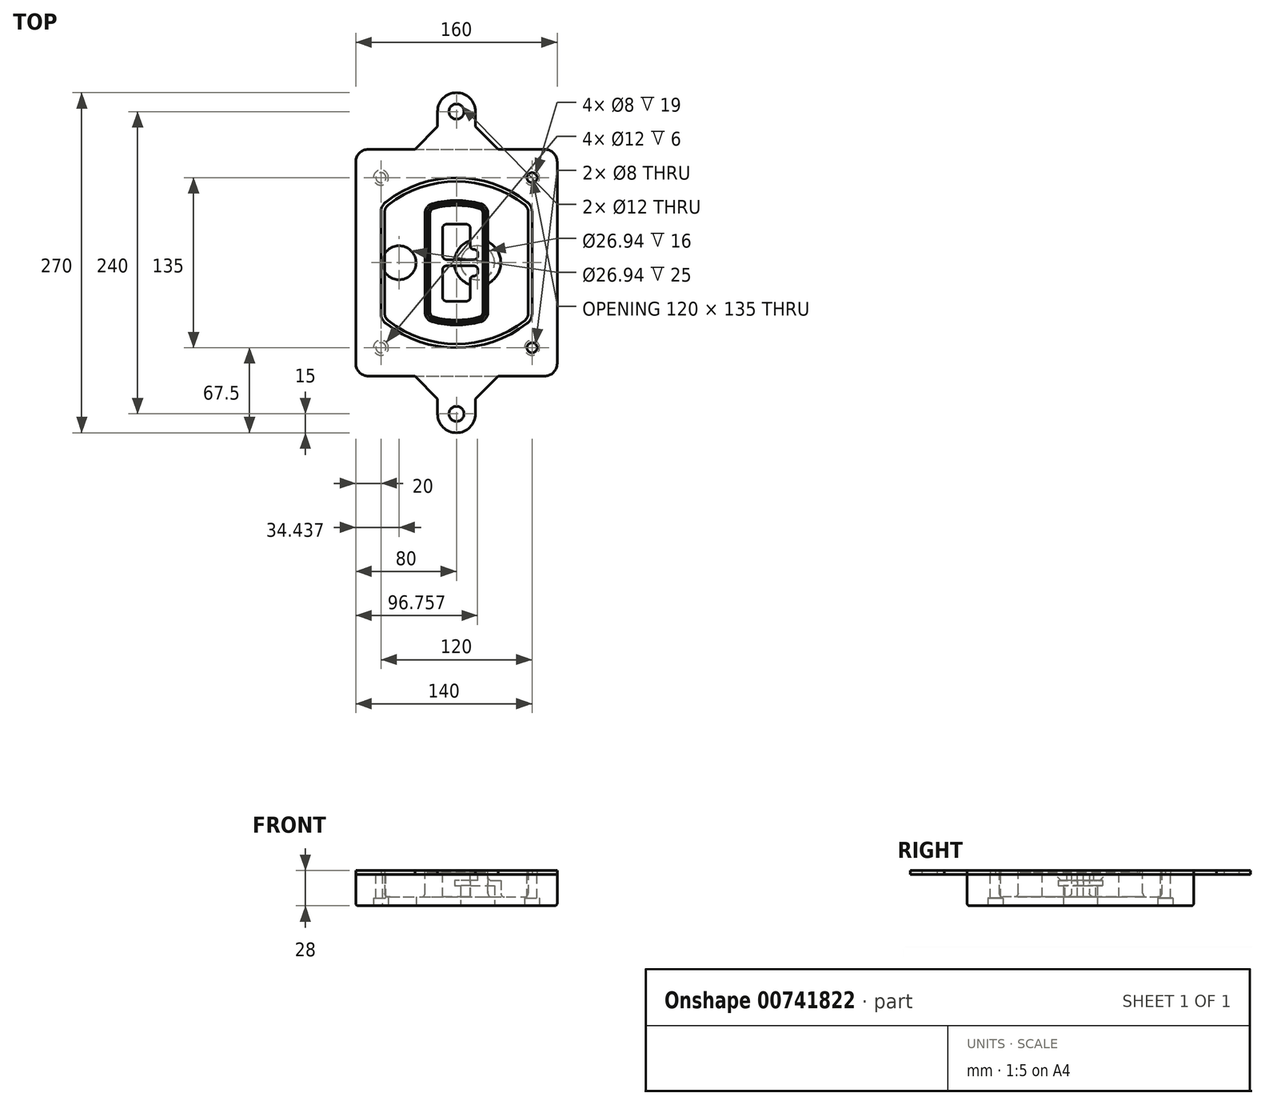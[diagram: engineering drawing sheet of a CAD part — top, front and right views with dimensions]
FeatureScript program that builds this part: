
annotation { "Feature Type Name" : "Feature", "Feature Type Description" : "" }
export const myFeature = defineFeature(function(context is Context, id is Id, definition is map)
    precondition{}
    {
        {
            var Q0;
            Q0=qCreatedBy(makeId("Top.planeOp"),FACE);
            var sketch = newSketch(context, id + "F0", { "sketchPlane" : qUnion([Q0])});
            skPoint(sketch, "E0.rect.middle", {"position": v(0, 0) * mm});
            skLineSegment(sketch, "E1.bottom", {"start": v(-70, -90) * mm, "end": v(70, -90) * mm});
            skLineSegment(sketch, "E1.top", {"start": v(-70, 90) * mm, "end": v(70, 90) * mm});
            skLineSegment(sketch, "E1.left", {"start": v(-80, -80) * mm, "end": v(-80, 80) * mm});
            skLineSegment(sketch, "E1.right", {"start": v(80, -80) * mm, "end": v(80, 80) * mm});
            skLineSegment(sketch, "E2", {"start": v(-80, 90) * mm, "end": v(80, -90) * mm, "construction": true});
            skLineSegment(sketch, "E3", {"start": v(80, 90) * mm, "end": v(-80, -90) * mm, "construction": true});
            skCircle(sketch, "E4", {"center": v(-60, 67.5) * mm, "radius": 4 * mm});
            skCircle(sketch, "E5", {"center": v(60, 67.5) * mm, "radius": 4 * mm});
            skCircle(sketch, "E6", {"center": v(60, -67.5) * mm, "radius": 4 * mm});
            skCircle(sketch, "E7", {"center": v(-60, -67.5) * mm, "radius": 4 * mm});
            skLineSegment(sketch, "E8", {"start": v(-60, 67.5) * mm, "end": v(60, 67.5) * mm, "construction": true});
            skLineSegment(sketch, "E9", {"start": v(60, 67.5) * mm, "end": v(60, -67.5) * mm, "construction": true});
            skLineSegment(sketch, "E10", {"start": v(60, -67.5) * mm, "end": v(-60, -67.5) * mm, "construction": true});
            skLineSegment(sketch, "E11", {"start": v(-60, -67.5) * mm, "end": v(-60, 67.5) * mm, "construction": true});
            skLineSegment(sketch, "E12", {"start": v(-60, 40.3) * mm, "end": v(-60, -40.3) * mm});
            skLineSegment(sketch, "E13", {"start": v(60, 40.3) * mm, "end": v(60, -40.3) * mm});
            skArc(sketch, "E14", {"start": v(56.15, 48.18) * mm, "mid": v(0, 67.5) * mm, "end": v(-56.15, 48.18) * mm});
            skArc(sketch, "E15", {"start": v(-56.15, -48.18) * mm, "mid": v(0, -67.5) * mm, "end": v(56.15, -48.18) * mm});
            skLineSegment(sketch, "E16", {"start": v(-60, 0) * mm, "end": v(60, 0) * mm, "construction": true});
            skPoint(sketch, "E17.visualSharp", {"position": v(-60, -45) * mm});
            skArc(sketch, "E17.filletArc", {"start": v(-60, -40.3) * mm, "mid": v(-58.99, -44.68) * mm, "end": v(-56.15, -48.18) * mm});
            skPoint(sketch, "E18.visualSharp", {"position": v(-60, 45) * mm});
            skArc(sketch, "E18.filletArc", {"start": v(-56.15, 48.18) * mm, "mid": v(-58.99, 44.68) * mm, "end": v(-60, 40.3) * mm});
            skPoint(sketch, "E19.visualSharp", {"position": v(60, 45) * mm});
            skArc(sketch, "E19.filletArc", {"start": v(60, 40.3) * mm, "mid": v(58.99, 44.68) * mm, "end": v(56.15, 48.18) * mm});
            skPoint(sketch, "E20.visualSharp", {"position": v(60, -45) * mm});
            skArc(sketch, "E20.filletArc", {"start": v(56.15, -48.18) * mm, "mid": v(58.99, -44.68) * mm, "end": v(60, -40.3) * mm});
            skPoint(sketch, "E21.visualSharp", {"position": v(-80, 90) * mm});
            skArc(sketch, "E21.filletArc", {"start": v(-70, 90) * mm, "mid": v(-77.07, 87.07) * mm, "end": v(-80, 80) * mm});
            skPoint(sketch, "E22.visualSharp", {"position": v(80, 90) * mm});
            skArc(sketch, "E22.filletArc", {"start": v(80, 80) * mm, "mid": v(77.07, 87.07) * mm, "end": v(70, 90) * mm});
            skPoint(sketch, "E23.visualSharp", {"position": v(80, -90) * mm});
            skArc(sketch, "E23.filletArc", {"start": v(70, -90) * mm, "mid": v(77.07, -87.07) * mm, "end": v(80, -80) * mm});
            skPoint(sketch, "E24.visualSharp", {"position": v(-80, -90) * mm});
            skArc(sketch, "E24.filletArc", {"start": v(-80, -80) * mm, "mid": v(-77.07, -87.07) * mm, "end": v(-70, -90) * mm});
            skArc(sketch, "E25.0", {"start": v(57, 40.3) * mm, "mid": v(56.3, 43.36) * mm, "end": v(54.3, 45.81) * mm});
            skLineSegment(sketch, "E25.1", {"start": v(57, 40.3) * mm, "end": v(57, -40.3) * mm});
            skArc(sketch, "E25.2", {"start": v(54.3, -45.81) * mm, "mid": v(56.3, -43.36) * mm, "end": v(57, -40.3) * mm});
            skArc(sketch, "E25.3", {"start": v(-54.3, -45.81) * mm, "mid": v(0, -64.5) * mm, "end": v(54.3, -45.81) * mm});
            skArc(sketch, "E25.4", {"start": v(-57, -40.3) * mm, "mid": v(-56.3, -43.36) * mm, "end": v(-54.3, -45.81) * mm});
            skArc(sketch, "E25.5", {"start": v(54.3, 45.81) * mm, "mid": v(0, 64.5) * mm, "end": v(-54.3, 45.81) * mm});
            skLineSegment(sketch, "E25.6", {"start": v(-57, 40.3) * mm, "end": v(-57, -40.3) * mm});
            skArc(sketch, "E25.7", {"start": v(-54.3, 45.81) * mm, "mid": v(-56.3, 43.36) * mm, "end": v(-57, 40.3) * mm});
            skArc(sketch, "E26.0", {"start": v(-58.62, 51.33) * mm, "mid": v(-62.58, 46.43) * mm, "end": v(-64, 40.3) * mm});
            skArc(sketch, "E26.1", {"start": v(58.62, 51.33) * mm, "mid": v(0, 71.5) * mm, "end": v(-58.62, 51.33) * mm});
            skArc(sketch, "E26.2", {"start": v(64, 40.3) * mm, "mid": v(62.58, 46.43) * mm, "end": v(58.62, 51.33) * mm});
            skLineSegment(sketch, "E26.3", {"start": v(64, 40.3) * mm, "end": v(64, -40.3) * mm});
            skArc(sketch, "E26.4", {"start": v(58.62, -51.33) * mm, "mid": v(62.58, -46.43) * mm, "end": v(64, -40.3) * mm});
            skLineSegment(sketch, "E26.5", {"start": v(-64, 40.3) * mm, "end": v(-64, -40.3) * mm});
            skArc(sketch, "E26.6", {"start": v(-58.62, -51.33) * mm, "mid": v(0, -71.5) * mm, "end": v(58.62, -51.33) * mm});
            skArc(sketch, "E26.7", {"start": v(-64, -40.3) * mm, "mid": v(-62.58, -46.43) * mm, "end": v(-58.62, -51.33) * mm});
            skSolve(sketch);
        }
        {
            var Q0;
            Q0=makeQuery(id+"F0.imprint","IMPRINT",FACE,{"disambiguationData":[TD([[makeQuery(id+"F0.imprint","IMPRINT",EDGE,{"derivedFrom":sQuery(id+"F0.wireOp",EDGE,"E1.bottom")}),1.0]])]});
            var Q1;
            Q1=makeQuery(id+"F0.imprint","IMPRINT",FACE,{"disambiguationData":[TD([[makeQuery(id+"F0.imprint","IMPRINT",EDGE,{"derivedFrom":sQuery(id+"F0.wireOp",EDGE,"E12")}),1.0]])]});
            var Q2;
            Q2=makeQuery(id+"F0.imprint","IMPRINT",FACE,{"disambiguationData":[TD([[makeQuery(id+"F0.imprint","IMPRINT",EDGE,{"derivedFrom":sQuery(id+"F0.wireOp",EDGE,"E25.0")}),1.0]])]});
            var Q3;
            Q3=makeQuery(id+"F0.imprint","IMPRINT",FACE,{"disambiguationData":[TD([[makeQuery(id+"F0.imprint","IMPRINT",EDGE,{"derivedFrom":sQuery(id+"F0.wireOp",EDGE,"E12")}),-1.0]])]});
            extrude(context, id + "F1", {"entities" : qUnion([Q0, Q1, Q2, Q3]), "oppositeDirection" : true, "depth" : 25 * mm});
        }
        {
            var Q0;
            Q0=makeQuery(id+"F0.imprint","IMPRINT",FACE,{"disambiguationData":[TD([[makeQuery(id+"F0.imprint","IMPRINT",EDGE,{"derivedFrom":sQuery(id+"F0.wireOp",EDGE,"E12")}),1.0]])]});
            extrude(context, id + "F2", {"entities" : qUnion([Q0]), "operationType" : NewBodyOperationType.ADD, "depth" : 3 * mm});
        }
        {
            var Q0;
            Q0=makeQuery(id+"F0.imprint","IMPRINT",FACE,{"disambiguationData":[TD([[makeQuery(id+"F0.imprint","IMPRINT",EDGE,{"derivedFrom":sQuery(id+"F0.wireOp",EDGE,"E25.0")}),1.0]])]});
            extrude(context, id + "F3", {"entities" : qUnion([Q0]), "operationType" : NewBodyOperationType.REMOVE, "oppositeDirection" : true, "depth" : 18 * mm});
        }
        {
            var Q0;
            Q0=makeQuery(id+"F2.opExtrude","CAP_FACE",FACE,{"disambiguationData":[OSD([sQuery(id+"F0.wireOp",EDGE,"E12"),sQuery(id+"F0.wireOp",EDGE,"E13"),sQuery(id+"F0.wireOp",EDGE,"E14"),sQuery(id+"F0.wireOp",EDGE,"E15"),sQuery(id+"F0.wireOp",EDGE,"E17.filletArc"),sQuery(id+"F0.wireOp",EDGE,"E18.filletArc"),sQuery(id+"F0.wireOp",EDGE,"E19.filletArc"),sQuery(id+"F0.wireOp",EDGE,"E20.filletArc"),sQuery(id+"F0.wireOp",EDGE,"E25.0"),sQuery(id+"F0.wireOp",EDGE,"E25.1"),sQuery(id+"F0.wireOp",EDGE,"E25.2"),sQuery(id+"F0.wireOp",EDGE,"E25.3"),sQuery(id+"F0.wireOp",EDGE,"E25.4"),sQuery(id+"F0.wireOp",EDGE,"E25.5"),sQuery(id+"F0.wireOp",EDGE,"E25.6"),sQuery(id+"F0.wireOp",EDGE,"E25.7")])],"isStart":false});
            var sketch = newSketch(context, id + "F4", { "sketchPlane" : qUnion([Q0])});
            skArc(sketch, "E27.0", {"start": v(-19.08, -46.97) * mm, "mid": v(0, -49.5) * mm, "end": v(19.08, -46.97) * mm});
            skArc(sketch, "E28.0", {"start": v(19.08, 46.97) * mm, "mid": v(0, 49.5) * mm, "end": v(-19.08, 46.97) * mm});
            skLineSegment(sketch, "E29", {"start": v(-25, 39.25) * mm, "end": v(-25, -39.25) * mm});
            skLineSegment(sketch, "E30", {"start": v(25, 39.25) * mm, "end": v(25, -39.25) * mm});
            skLineSegment(sketch, "E31", {"start": v(-25, 45.1) * mm, "end": v(25, 45.1) * mm, "construction": true});
            skLineSegment(sketch, "E32", {"start": v(-25, -45.1) * mm, "end": v(25, -45.1) * mm, "construction": true});
            skPoint(sketch, "E33.visualSharp", {"position": v(-25, 45.1) * mm});
            skArc(sketch, "E33.filletArc", {"start": v(-19.08, 46.97) * mm, "mid": v(-23.35, 44.11) * mm, "end": v(-25, 39.25) * mm});
            skPoint(sketch, "E34.visualSharp", {"position": v(25, 45.1) * mm});
            skArc(sketch, "E34.filletArc", {"start": v(25, 39.25) * mm, "mid": v(23.35, 44.11) * mm, "end": v(19.08, 46.97) * mm});
            skPoint(sketch, "E35.visualSharp", {"position": v(25, -45.1) * mm});
            skArc(sketch, "E35.filletArc", {"start": v(19.08, -46.97) * mm, "mid": v(23.35, -44.11) * mm, "end": v(25, -39.25) * mm});
            skPoint(sketch, "E36.visualSharp", {"position": v(-25, -45.1) * mm});
            skArc(sketch, "E36.filletArc", {"start": v(-25, -39.25) * mm, "mid": v(-23.35, -44.11) * mm, "end": v(-19.08, -46.97) * mm});
            skArc(sketch, "E37.0", {"start": v(54.3, 45.81) * mm, "mid": v(0, 64.5) * mm, "end": v(-54.3, 45.81) * mm});
            skArc(sketch, "E37.1", {"start": v(-54.3, 45.81) * mm, "mid": v(-56.3, 43.36) * mm, "end": v(-57, 40.3) * mm});
            skLineSegment(sketch, "E37.2", {"start": v(-57, 40.3) * mm, "end": v(-57, -40.3) * mm});
            skArc(sketch, "E37.3", {"start": v(-57, -40.3) * mm, "mid": v(-56.3, -43.36) * mm, "end": v(-54.3, -45.81) * mm});
            skArc(sketch, "E37.4", {"start": v(-54.3, -45.81) * mm, "mid": v(0, -64.5) * mm, "end": v(54.3, -45.81) * mm});
            skArc(sketch, "E37.5", {"start": v(54.3, -45.81) * mm, "mid": v(56.3, -43.36) * mm, "end": v(57, -40.3) * mm});
            skLineSegment(sketch, "E37.6", {"start": v(57, 40.3) * mm, "end": v(57, -40.3) * mm});
            skArc(sketch, "E37.7", {"start": v(57, 40.3) * mm, "mid": v(56.3, 43.36) * mm, "end": v(54.3, 45.81) * mm});
            skLineSegment(sketch, "E38.0", {"start": v(23, 39.25) * mm, "end": v(23, -39.25) * mm});
            skArc(sketch, "E38.1", {"start": v(18.56, -45.04) * mm, "mid": v(21.76, -42.9) * mm, "end": v(23, -39.25) * mm});
            skArc(sketch, "E38.2", {"start": v(-18.56, -45.04) * mm, "mid": v(0, -47.5) * mm, "end": v(18.56, -45.04) * mm});
            skArc(sketch, "E38.3", {"start": v(-23, -39.25) * mm, "mid": v(-21.76, -42.9) * mm, "end": v(-18.56, -45.04) * mm});
            skLineSegment(sketch, "E38.4", {"start": v(-23, 39.25) * mm, "end": v(-23, -39.25) * mm});
            skArc(sketch, "E38.5", {"start": v(23, 39.25) * mm, "mid": v(21.76, 42.9) * mm, "end": v(18.56, 45.04) * mm});
            skArc(sketch, "E38.6", {"start": v(-18.56, 45.04) * mm, "mid": v(-21.76, 42.9) * mm, "end": v(-23, 39.25) * mm});
            skArc(sketch, "E38.7", {"start": v(18.56, 45.04) * mm, "mid": v(0, 47.5) * mm, "end": v(-18.56, 45.04) * mm});
            skArc(sketch, "E39.0", {"start": v(21, 39.25) * mm, "mid": v(20.18, 41.68) * mm, "end": v(18.04, 43.1) * mm});
            skLineSegment(sketch, "E39.1", {"start": v(21, 39.25) * mm, "end": v(21, -39.25) * mm});
            skArc(sketch, "E39.2", {"start": v(18.04, -43.1) * mm, "mid": v(20.18, -41.68) * mm, "end": v(21, -39.25) * mm});
            skArc(sketch, "E39.3", {"start": v(-18.04, -43.1) * mm, "mid": v(0, -45.5) * mm, "end": v(18.04, -43.1) * mm});
            skArc(sketch, "E39.4", {"start": v(-21, -39.25) * mm, "mid": v(-20.18, -41.68) * mm, "end": v(-18.04, -43.1) * mm});
            skArc(sketch, "E39.5", {"start": v(18.04, 43.1) * mm, "mid": v(0, 45.5) * mm, "end": v(-18.04, 43.1) * mm});
            skLineSegment(sketch, "E39.6", {"start": v(-21, 39.25) * mm, "end": v(-21, -39.25) * mm});
            skArc(sketch, "E39.7", {"start": v(-18.04, 43.1) * mm, "mid": v(-20.18, 41.68) * mm, "end": v(-21, 39.25) * mm});
            skLineSegment(sketch, "E40", {"start": v(-25, 0) * mm, "end": v(25, 0) * mm, "construction": true});
            skLineSegment(sketch, "E41", {"start": v(-11, 5.5) * mm, "end": v(-11, 27.5) * mm});
            skLineSegment(sketch, "E42", {"start": v(-8, 30.5) * mm, "end": v(8, 30.5) * mm});
            skLineSegment(sketch, "E43", {"start": v(11, 27.5) * mm, "end": v(11, 13.5) * mm});
            skLineSegment(sketch, "E44", {"start": v(14, 10.5) * mm, "end": v(14, 10.5) * mm});
            skLineSegment(sketch, "E45", {"start": v(17, 7.5) * mm, "end": v(17, 5.5) * mm});
            skLineSegment(sketch, "E46", {"start": v(14, 2.5) * mm, "end": v(-8, 2.5) * mm});
            skPoint(sketch, "E47.visualSharp", {"position": v(-11, 30.5) * mm});
            skArc(sketch, "E47.filletArc", {"start": v(-8, 30.5) * mm, "mid": v(-10.12, 29.62) * mm, "end": v(-11, 27.5) * mm});
            skPoint(sketch, "E48.visualSharp", {"position": v(11, 30.5) * mm});
            skArc(sketch, "E48.filletArc", {"start": v(11, 27.5) * mm, "mid": v(10.12, 29.62) * mm, "end": v(8, 30.5) * mm});
            skPoint(sketch, "E49.visualSharp", {"position": v(11, 10.5) * mm});
            skArc(sketch, "E49.filletArc", {"start": v(11, 13.5) * mm, "mid": v(11.88, 11.38) * mm, "end": v(14, 10.5) * mm});
            skPoint(sketch, "E50.visualSharp", {"position": v(17, 10.5) * mm});
            skArc(sketch, "E50.filletArc", {"start": v(17, 7.5) * mm, "mid": v(16.12, 9.62) * mm, "end": v(14, 10.5) * mm});
            skPoint(sketch, "E51.visualSharp", {"position": v(17, 2.5) * mm});
            skArc(sketch, "E51.filletArc", {"start": v(14, 2.5) * mm, "mid": v(16.12, 3.38) * mm, "end": v(17, 5.5) * mm});
            skPoint(sketch, "E52.visualSharp", {"position": v(-11, 2.5) * mm});
            skArc(sketch, "E52.filletArc", {"start": v(-11, 5.5) * mm, "mid": v(-10.12, 3.38) * mm, "end": v(-8, 2.5) * mm});
            skLineSegment(sketch, "E53.0.MirrorCS", {"start": v(14, -2.5) * mm, "end": v(-8, -2.5) * mm});
            skArc(sketch, "E54.0.MirrorCS", {"start": v(-11, -5.5) * mm, "mid": v(-10.12, -3.38) * mm, "end": v(-8, -2.5) * mm});
            skLineSegment(sketch, "E55.0.MirrorCS", {"start": v(-11, -5.5) * mm, "end": v(-11, -27.5) * mm});
            skArc(sketch, "E56.0.MirrorCS", {"start": v(-8, -30.5) * mm, "mid": v(-10.12, -29.62) * mm, "end": v(-11, -27.5) * mm});
            skLineSegment(sketch, "E57.0.MirrorCS", {"start": v(-8, -30.5) * mm, "end": v(8, -30.5) * mm});
            skArc(sketch, "E58.0.MirrorCS", {"start": v(11, -27.5) * mm, "mid": v(10.12, -29.62) * mm, "end": v(8, -30.5) * mm});
            skLineSegment(sketch, "E59.0.MirrorCS", {"start": v(11, -27.5) * mm, "end": v(11, -13.5) * mm});
            skArc(sketch, "E60.0.MirrorCS", {"start": v(11, -13.5) * mm, "mid": v(11.88, -11.38) * mm, "end": v(14, -10.5) * mm});
            skArc(sketch, "E61.0.MirrorCS", {"start": v(17, -7.5) * mm, "mid": v(16.12, -9.62) * mm, "end": v(14, -10.5) * mm});
            skLineSegment(sketch, "E62.0.MirrorCS", {"start": v(17, -7.5) * mm, "end": v(17, -5.5) * mm});
            skArc(sketch, "E63.0.MirrorCS", {"start": v(14, -2.5) * mm, "mid": v(16.12, -3.38) * mm, "end": v(17, -5.5) * mm});
            skSolve(sketch);
        }
        {
            var Q0;
            Q0=makeQuery(id+"F4.imprint","IMPRINT",FACE,{"disambiguationData":[TD([[makeQuery(id+"F4.imprint","IMPRINT",EDGE,{"derivedFrom":sQuery(id+"F4.wireOp",EDGE,"E27.0")}),1.0]])]});
            var Q1;
            Q1=makeQuery(id+"F4.imprint","IMPRINT",FACE,{"disambiguationData":[TD([[makeQuery(id+"F4.imprint","IMPRINT",EDGE,{"derivedFrom":sQuery(id+"F4.wireOp",EDGE,"E38.0")}),-1.0]])]});
            var Q2;
            Q2=makeQuery(id+"F4.imprint","IMPRINT",FACE,{"disambiguationData":[TD([[makeQuery(id+"F4.imprint","IMPRINT",EDGE,{"derivedFrom":sQuery(id+"F4.wireOp",EDGE,"E39.0")}),1.0]])]});
            extrude(context, id + "F5", {"entities" : qUnion([Q0, Q1, Q2]), "operationType" : NewBodyOperationType.ADD, "endBound" : BoundingType.UP_TO_NEXT, "oppositeDirection" : true, "depth" : 25 * mm});
        }
        {
            var Q0;
            Q0=makeQuery(id+"F4.imprint","IMPRINT",FACE,{"disambiguationData":[TD([[makeQuery(id+"F4.imprint","IMPRINT",EDGE,{"derivedFrom":sQuery(id+"F4.wireOp",EDGE,"E38.0")}),-1.0]])]});
            extrude(context, id + "F6", {"entities" : qUnion([Q0]), "operationType" : NewBodyOperationType.REMOVE, "oppositeDirection" : true, "depth" : 2 * mm});
        }
        {
            var Q0;
            Q0=makeQuery(id+"F1.opExtrude","CAP_FACE",FACE,{"disambiguationData":[OSD([sQuery(id+"F0.wireOp",EDGE,"E1.bottom"),sQuery(id+"F0.wireOp",EDGE,"E1.top"),sQuery(id+"F0.wireOp",EDGE,"E1.left"),sQuery(id+"F0.wireOp",EDGE,"E1.right"),sQuery(id+"F0.wireOp",EDGE,"E4"),sQuery(id+"F0.wireOp",EDGE,"E5"),sQuery(id+"F0.wireOp",EDGE,"E6"),sQuery(id+"F0.wireOp",EDGE,"E7"),sQuery(id+"F0.wireOp",EDGE,"E21.filletArc"),sQuery(id+"F0.wireOp",EDGE,"E22.filletArc"),sQuery(id+"F0.wireOp",EDGE,"E23.filletArc"),sQuery(id+"F0.wireOp",EDGE,"E24.filletArc")])],"isStart":false});
            var sketch = newSketch(context, id + "F7", { "sketchPlane" : qUnion([Q0])});
            skCircle(sketch, "E64", {"center": v(16.76, 0) * mm, "radius": 13.47 * mm});
            skCircle(sketch, "E65", {"center": v(-45.56, 0) * mm, "radius": 13.47 * mm});
            skLineSegment(sketch, "E66", {"start": v(80, 0) * mm, "end": v(-80, 0) * mm});
            skCircle(sketch, "E67", {"center": v(16.76, 0) * mm, "radius": 18.47 * mm});
            skCircle(sketch, "E68", {"center": v(60, -67.5) * mm, "radius": 6 * mm});
            skCircle(sketch, "E69", {"center": v(-60, -67.5) * mm, "radius": 6 * mm});
            skCircle(sketch, "E70", {"center": v(-60, 67.5) * mm, "radius": 6 * mm});
            skCircle(sketch, "E71", {"center": v(60, 67.5) * mm, "radius": 6 * mm});
            skSolve(sketch);
        }
        {
            var Q0;
            {var subQ1=sQuery(id+"F7.wireOp",EDGE,"E66");var subQ4=sQuery(id+"F7.wireOp",EDGE,"E64");var subQ6=makeQuery(id+"F7.imprint","INTERSECT",VERTEX,{"disambiguationData":[OD(0.0)],"derivedFrom":[subQ4,subQ1]});Q0=makeQuery(id+"F7.imprint","IMPRINT",FACE,{"disambiguationData":[TD([[makeQuery(id+"F7.imprint","IMPRINT",EDGE,{"disambiguationData":[TD([[subQ6,-1.0]])],"derivedFrom":subQ4}),-1.0]])]});}
            var Q1;
            {var subQ0=sQuery(id+"F7.wireOp",EDGE,"E66");var subQ1=sQuery(id+"F7.wireOp",EDGE,"E64");var subQ3=makeQuery(id+"F7.imprint","INTERSECT",VERTEX,{"disambiguationData":[OD(0.0)],"derivedFrom":[subQ1,subQ0]});Q1=makeQuery(id+"F7.imprint","IMPRINT",FACE,{"disambiguationData":[TD([[makeQuery(id+"F7.imprint","IMPRINT",EDGE,{"disambiguationData":[TD([[subQ3,-1.0]])],"derivedFrom":subQ1}),1.0]])]});}
            var Q2;
            {var subQ0=sQuery(id+"F7.wireOp",EDGE,"E66");var subQ1=sQuery(id+"F7.wireOp",EDGE,"E64");var subQ3=makeQuery(id+"F7.imprint","INTERSECT",VERTEX,{"disambiguationData":[OD(0.0)],"derivedFrom":[subQ1,subQ0]});Q2=makeQuery(id+"F7.imprint","IMPRINT",FACE,{"disambiguationData":[TD([[makeQuery(id+"F7.imprint","IMPRINT",EDGE,{"disambiguationData":[TD([[subQ3,1.0]])],"derivedFrom":subQ1}),1.0]])]});}
            var Q3;
            {var subQ1=sQuery(id+"F7.wireOp",EDGE,"E66");var subQ4=sQuery(id+"F7.wireOp",EDGE,"E64");var subQ6=makeQuery(id+"F7.imprint","INTERSECT",VERTEX,{"disambiguationData":[OD(0.0)],"derivedFrom":[subQ4,subQ1]});Q3=makeQuery(id+"F7.imprint","IMPRINT",FACE,{"disambiguationData":[TD([[makeQuery(id+"F7.imprint","IMPRINT",EDGE,{"disambiguationData":[TD([[subQ6,1.0]])],"derivedFrom":subQ4}),-1.0]])]});}
            extrude(context, id + "F8", {"entities" : qUnion([Q0, Q1, Q2, Q3]), "operationType" : NewBodyOperationType.ADD, "oppositeDirection" : true, "depth" : 20 * mm});
        }
        {
            var Q0;
            {var subQ0=sQuery(id+"F7.wireOp",EDGE,"E66");var subQ1=sQuery(id+"F7.wireOp",EDGE,"E64");var subQ3=makeQuery(id+"F7.imprint","INTERSECT",VERTEX,{"disambiguationData":[OD(0.0)],"derivedFrom":[subQ1,subQ0]});Q0=makeQuery(id+"F7.imprint","IMPRINT",FACE,{"disambiguationData":[TD([[makeQuery(id+"F7.imprint","IMPRINT",EDGE,{"disambiguationData":[TD([[subQ3,-1.0]])],"derivedFrom":subQ1}),1.0]])]});}
            var Q1;
            {var subQ0=sQuery(id+"F7.wireOp",EDGE,"E66");var subQ1=sQuery(id+"F7.wireOp",EDGE,"E64");var subQ3=makeQuery(id+"F7.imprint","INTERSECT",VERTEX,{"disambiguationData":[OD(0.0)],"derivedFrom":[subQ1,subQ0]});Q1=makeQuery(id+"F7.imprint","IMPRINT",FACE,{"disambiguationData":[TD([[makeQuery(id+"F7.imprint","IMPRINT",EDGE,{"disambiguationData":[TD([[subQ3,1.0]])],"derivedFrom":subQ1}),1.0]])]});}
            extrude(context, id + "F9", {"entities" : qUnion([Q0, Q1]), "operationType" : NewBodyOperationType.REMOVE, "oppositeDirection" : true, "depth" : 16 * mm});
        }
        {
            var Q0;
            {var subQ0=sQuery(id+"F7.wireOp",EDGE,"E66");var subQ1=sQuery(id+"F7.wireOp",EDGE,"E65");var subQ3=makeQuery(id+"F7.imprint","INTERSECT",VERTEX,{"disambiguationData":[OD(0.0)],"derivedFrom":[subQ1,subQ0]});Q0=makeQuery(id+"F7.imprint","IMPRINT",FACE,{"disambiguationData":[TD([[makeQuery(id+"F7.imprint","IMPRINT",EDGE,{"disambiguationData":[TD([[subQ3,-1.0]])],"derivedFrom":subQ1}),1.0]])]});}
            var Q1;
            {var subQ0=sQuery(id+"F7.wireOp",EDGE,"E66");var subQ1=sQuery(id+"F7.wireOp",EDGE,"E65");var subQ3=makeQuery(id+"F7.imprint","INTERSECT",VERTEX,{"disambiguationData":[OD(0.0)],"derivedFrom":[subQ1,subQ0]});Q1=makeQuery(id+"F7.imprint","IMPRINT",FACE,{"disambiguationData":[TD([[makeQuery(id+"F7.imprint","IMPRINT",EDGE,{"disambiguationData":[TD([[subQ3,1.0]])],"derivedFrom":subQ1}),1.0]])]});}
            extrude(context, id + "F10", {"entities" : qUnion([Q0, Q1]), "operationType" : NewBodyOperationType.REMOVE, "oppositeDirection" : true, "depth" : 25 * mm});
        }
        {
            var Q0;
            Q0=makeQuery(id+"F7.imprint","IMPRINT",FACE,{"disambiguationData":[TD([[makeQuery(id+"F7.imprint","IMPRINT",EDGE,{"derivedFrom":sQuery(id+"F7.wireOp",EDGE,"E68")}),1.0]])]});
            var Q1;
            Q1=makeQuery(id+"F7.imprint","IMPRINT",FACE,{"disambiguationData":[TD([[makeQuery(id+"F7.imprint","IMPRINT",EDGE,{"derivedFrom":makeQuery(id+"F1.opExtrude","CAP_EDGE",EDGE,{"disambiguationData":[OSD([sQuery(id+"F0.wireOp",EDGE,"E5")])],"isStart":false})}),-1.0]])]});
            var Q2;
            Q2=makeQuery(id+"F7.imprint","IMPRINT",FACE,{"disambiguationData":[TD([[makeQuery(id+"F7.imprint","IMPRINT",EDGE,{"derivedFrom":sQuery(id+"F7.wireOp",EDGE,"E69")}),1.0]])]});
            var Q3;
            Q3=makeQuery(id+"F7.imprint","IMPRINT",FACE,{"disambiguationData":[TD([[makeQuery(id+"F7.imprint","IMPRINT",EDGE,{"derivedFrom":makeQuery(id+"F1.opExtrude","CAP_EDGE",EDGE,{"disambiguationData":[OSD([sQuery(id+"F0.wireOp",EDGE,"E4")])],"isStart":false})}),-1.0]])]});
            var Q4;
            Q4=makeQuery(id+"F7.imprint","IMPRINT",FACE,{"disambiguationData":[TD([[makeQuery(id+"F7.imprint","IMPRINT",EDGE,{"derivedFrom":sQuery(id+"F7.wireOp",EDGE,"E70")}),1.0]])]});
            var Q5;
            Q5=makeQuery(id+"F7.imprint","IMPRINT",FACE,{"disambiguationData":[TD([[makeQuery(id+"F7.imprint","IMPRINT",EDGE,{"derivedFrom":makeQuery(id+"F1.opExtrude","CAP_EDGE",EDGE,{"disambiguationData":[OSD([sQuery(id+"F0.wireOp",EDGE,"E7")])],"isStart":false})}),-1.0]])]});
            var Q6;
            Q6=makeQuery(id+"F7.imprint","IMPRINT",FACE,{"disambiguationData":[TD([[makeQuery(id+"F7.imprint","IMPRINT",EDGE,{"derivedFrom":sQuery(id+"F7.wireOp",EDGE,"E71")}),1.0]])]});
            var Q7;
            Q7=makeQuery(id+"F7.imprint","IMPRINT",FACE,{"disambiguationData":[TD([[makeQuery(id+"F7.imprint","IMPRINT",EDGE,{"derivedFrom":makeQuery(id+"F1.opExtrude","CAP_EDGE",EDGE,{"disambiguationData":[OSD([sQuery(id+"F0.wireOp",EDGE,"E6")])],"isStart":false})}),-1.0]])]});
            extrude(context, id + "F11", {"entities" : qUnion([Q0, Q1, Q2, Q3, Q4, Q5, Q6, Q7]), "operationType" : NewBodyOperationType.REMOVE, "oppositeDirection" : true, "depth" : 6 * mm});
        }
        {
            var Q0;
            Q0=makeQuery(id+"F9.boolean.opBoolean","COPY",FACE,{"derivedFrom":makeQuery(id+"F9.opExtrude","CAP_FACE",FACE,{"disambiguationData":[OSD([sQuery(id+"F7.wireOp",EDGE,"E64")])],"isStart":false})});
            var sketch = newSketch(context, id + "F12", { "sketchPlane" : qUnion([Q0])});
            skArc(sketch, "E72.0", {"start": v(11, 17.55) * mm, "mid": v(2.57, 11.82) * mm, "end": v(-1.54, 2.5) * mm});
            skArc(sketch, "E72.1", {"start": v(-1.54, -2.5) * mm, "mid": v(2.57, -11.82) * mm, "end": v(11, -17.55) * mm});
            skLineSegment(sketch, "E73", {"start": v(-1.54, -2.5) * mm, "end": v(14, -2.5) * mm});
            skLineSegment(sketch, "E74.0", {"start": v(14, 2.5) * mm, "end": v(-1.54, 2.5) * mm});
            skArc(sketch, "E74.1", {"start": v(14, 2.5) * mm, "mid": v(16.12, 3.38) * mm, "end": v(17, 5.5) * mm});
            skLineSegment(sketch, "E74.2", {"start": v(17, 7.5) * mm, "end": v(17, 5.5) * mm});
            skArc(sketch, "E74.3", {"start": v(17, 7.5) * mm, "mid": v(16.12, 9.62) * mm, "end": v(14, 10.5) * mm});
            skArc(sketch, "E74.4", {"start": v(11, 13.5) * mm, "mid": v(11.88, 11.38) * mm, "end": v(14, 10.5) * mm});
            skLineSegment(sketch, "E74.5", {"start": v(11, 17.55) * mm, "end": v(11, 13.5) * mm});
            skLineSegment(sketch, "E74.7", {"start": v(14, -2.5) * mm, "end": v(-1.54, -2.5) * mm});
            skArc(sketch, "E74.8", {"start": v(14, -2.5) * mm, "mid": v(16.12, -3.38) * mm, "end": v(17, -5.5) * mm});
            skLineSegment(sketch, "E74.9", {"start": v(17, -7.5) * mm, "end": v(17, -5.5) * mm});
            skArc(sketch, "E74.10", {"start": v(17, -7.5) * mm, "mid": v(16.12, -9.62) * mm, "end": v(14, -10.5) * mm});
            skArc(sketch, "E74.11", {"start": v(11, -13.5) * mm, "mid": v(11.88, -11.38) * mm, "end": v(14, -10.5) * mm});
            skLineSegment(sketch, "E74.12", {"start": v(11, -17.55) * mm, "end": v(11, -13.5) * mm});
            skPoint(sketch, "E75.orphan", {"position": v(11, -27.5) * mm});
            skPoint(sketch, "E76.orphan", {"position": v(-8, -2.5) * mm});
            skPoint(sketch, "E77.orphan", {"position": v(-8, 2.5) * mm});
            skPoint(sketch, "E78.orphan", {"position": v(11, 27.5) * mm});
            skSolve(sketch);
        }
        {
            var Q0;
            {var subQ7=sQuery(id+"F12.wireOp",EDGE,"E72.0");var subQ14=sQuery(id+"F12.wireOp",EDGE,"E72.1");var subQ16=sQuery(id+"F12.wireOp",EDGE,"E74.1");var subQ18=sQuery(id+"F12.wireOp",EDGE,"E74.8");Q0=qUnion([makeQuery(id+"F12.imprint","IMPRINT",FACE,{"disambiguationData":[TD([[makeQuery(id+"F12.imprint","IMPRINT",EDGE,{"derivedFrom":subQ7}),1.0]])]}),makeQuery(id+"F12.imprint","IMPRINT",FACE,{"disambiguationData":[TD([[makeQuery(id+"F12.imprint","IMPRINT",EDGE,{"derivedFrom":subQ14}),1.0]])]}),makeQuery(id+"F12.imprint","IMPRINT",FACE,{"disambiguationData":[TD([[makeQuery(id+"F12.imprint","IMPRINT",EDGE,{"derivedFrom":subQ16}),1.0]])]}),makeQuery(id+"F12.imprint","IMPRINT",FACE,{"disambiguationData":[TD([[makeQuery(id+"F12.imprint","IMPRINT",EDGE,{"derivedFrom":subQ18}),-1.0]])]})]);}
            var Q1;
            Q1=makeQuery(id+"F5.boolean.opBoolean","SPLIT",FACE,{"disambiguationData":[TD([makeQuery(id+"F5.opExtrude","SWEPT_FACE",FACE,{"disambiguationData":[OSD([sQuery(id+"F4.wireOp",EDGE,"E41")])]})])],"derivedFrom":makeQuery(id+"F3.boolean.opBoolean","COPY",FACE,{"derivedFrom":makeQuery(id+"F3.opExtrude","CAP_FACE",FACE,{"disambiguationData":[OSD([sQuery(id+"F0.wireOp",EDGE,"E25.0"),sQuery(id+"F0.wireOp",EDGE,"E25.1"),sQuery(id+"F0.wireOp",EDGE,"E25.2"),sQuery(id+"F0.wireOp",EDGE,"E25.3"),sQuery(id+"F0.wireOp",EDGE,"E25.4"),sQuery(id+"F0.wireOp",EDGE,"E25.5"),sQuery(id+"F0.wireOp",EDGE,"E25.6"),sQuery(id+"F0.wireOp",EDGE,"E25.7")])],"isStart":false})})});
            extrude(context, id + "F13", {"entities" : qUnion([Q0]), "operationType" : NewBodyOperationType.REMOVE, "endBound" : BoundingType.UP_TO_SURFACE, "endBoundEntityFace" : qUnion([Q1]), "depth" : 25 * mm});
        }
        {
            var Q0;
            Q0=makeQuery(id+"F3.boolean.opBoolean","COPY",EDGE,{"derivedFrom":makeQuery(id+"F3.opExtrude","CAP_EDGE",EDGE,{"disambiguationData":[OSD([sQuery(id+"F0.wireOp",EDGE,"E25.6")])],"isStart":false})});
            var Q1;
            Q1=makeQuery(id+"F8.boolean.opBoolean","INTERSECT",EDGE,{"derivedFrom":[makeQuery(id+"F5.opExtrude","SWEPT_FACE",FACE,{"disambiguationData":[OSD([sQuery(id+"F4.wireOp",EDGE,"E30")])]}),makeQuery(id+"F8.opExtrude","CAP_FACE",FACE,{"disambiguationData":[OSD([sQuery(id+"F7.wireOp",EDGE,"E67")])],"isStart":false})]});
            var Q2;
            Q2=makeQuery(id+"F8.boolean.opBoolean","INTERSECT",EDGE,{"disambiguationData":[OD(1.0)],"derivedFrom":[makeQuery(id+"F5.opExtrude","SWEPT_FACE",FACE,{"disambiguationData":[OSD([sQuery(id+"F4.wireOp",EDGE,"E30")])]}),makeQuery(id+"F8.opExtrude","SWEPT_FACE",FACE,{"disambiguationData":[OSD([sQuery(id+"F7.wireOp",EDGE,"E67")])]})]});
            var Q3;
            {var subQ0=sQuery(id+"F4.wireOp",EDGE,"E30");Q3=makeQuery(id+"F8.boolean.opBoolean","SPLIT",EDGE,{"disambiguationData":[TD([makeQuery(id+"F5.opExtrude","SWEPT_FACE",FACE,{"disambiguationData":[OSD([sQuery(id+"F4.wireOp",EDGE,"E35.filletArc")])]})])],"derivedFrom":makeQuery(id+"F5.opExtrude","CAP_EDGE",EDGE,{"disambiguationData":[OSD([subQ0])],"isStart":false})});}
            var Q4;
            {var subQ0=sQuery(id+"F0.wireOp",EDGE,"E25.7");var subQ1=sQuery(id+"F0.wireOp",EDGE,"E25.1");var subQ2=sQuery(id+"F0.wireOp",EDGE,"E25.6");var subQ3=sQuery(id+"F0.wireOp",EDGE,"E25.5");var subQ4=sQuery(id+"F0.wireOp",EDGE,"E25.4");var subQ5=sQuery(id+"F0.wireOp",EDGE,"E25.0");var subQ6=sQuery(id+"F0.wireOp",EDGE,"E25.2");var subQ7=sQuery(id+"F0.wireOp",EDGE,"E25.3");Q4=makeQuery(id+"F8.boolean.opBoolean","INTERSECT",EDGE,{"derivedFrom":[makeQuery(id+"F5.boolean.opBoolean","SPLIT",FACE,{"disambiguationData":[TD([makeQuery(id+"F2.opExtrude","SWEPT_FACE",FACE,{"disambiguationData":[OSD([subQ5])]})])],"derivedFrom":makeQuery(id+"F3.boolean.opBoolean","COPY",FACE,{"derivedFrom":makeQuery(id+"F3.opExtrude","CAP_FACE",FACE,{"disambiguationData":[OSD([subQ5,subQ1,subQ6,subQ7,subQ4,subQ3,subQ2,subQ0])],"isStart":false})})}),makeQuery(id+"F8.opExtrude","SWEPT_FACE",FACE,{"disambiguationData":[OSD([sQuery(id+"F7.wireOp",EDGE,"E67")])]})]});}
            var Q5;
            Q5=makeQuery(id+"F8.boolean.opBoolean","INTERSECT",EDGE,{"disambiguationData":[OD(0.0)],"derivedFrom":[makeQuery(id+"F5.opExtrude","SWEPT_FACE",FACE,{"disambiguationData":[OSD([sQuery(id+"F4.wireOp",EDGE,"E30")])]}),makeQuery(id+"F8.opExtrude","SWEPT_FACE",FACE,{"disambiguationData":[OSD([sQuery(id+"F7.wireOp",EDGE,"E67")])]})]});
            fillet(context, id + "F14", {"entities" : qUnion([Q0, Q1, Q2, Q3, Q4, Q5]), "radius" : 3 * mm, "tangentPropagation" : true, "allowEdgeOverflow" : false});
        }
        {
            var Q0;
            Q0=makeQuery(id+"F1.opExtrude","CAP_EDGE",EDGE,{"disambiguationData":[OSD([sQuery(id+"F0.wireOp",EDGE,"E1.bottom")])],"isStart":false});
            fillet(context, id + "F15", {"entities" : qUnion([Q0]), "radius" : 2 * mm, "tangentPropagation" : true, "allowEdgeOverflow" : false});
        }
        {
            var Q0;
            {var subQ0=sQuery(id+"F0.wireOp",EDGE,"E21.filletArc");var subQ1=sQuery(id+"F0.wireOp",EDGE,"E7");var subQ2=sQuery(id+"F0.wireOp",EDGE,"E6");var subQ3=sQuery(id+"F0.wireOp",EDGE,"E5");var subQ4=sQuery(id+"F0.wireOp",EDGE,"E4");var subQ5=sQuery(id+"F0.wireOp",EDGE,"E22.filletArc");var subQ6=sQuery(id+"F0.wireOp",EDGE,"E1.bottom");var subQ7=sQuery(id+"F0.wireOp",EDGE,"E1.right");var subQ8=sQuery(id+"F0.wireOp",EDGE,"E1.top");var subQ9=sQuery(id+"F0.wireOp",EDGE,"E1.left");var subQ10=sQuery(id+"F0.wireOp",EDGE,"E23.filletArc");var subQ11=sQuery(id+"F0.wireOp",EDGE,"E24.filletArc");Q0=makeQuery(id+"F2.boolean.opBoolean","SPLIT",FACE,{"disambiguationData":[TD([makeQuery(id+"F1.opExtrude","SWEPT_FACE",FACE,{"disambiguationData":[OSD([subQ6])]})])],"derivedFrom":makeQuery(id+"F1.opExtrude","CAP_FACE",FACE,{"disambiguationData":[OSD([subQ6,subQ8,subQ9,subQ7,subQ4,subQ3,subQ2,subQ1,subQ0,subQ5,subQ10,subQ11])],"isStart":true})});}
            var sketch = newSketch(context, id + "F16", { "sketchPlane" : qUnion([Q0])});
            skLineSegment(sketch, "E79.0", {"start": v(-80, -80) * mm, "end": v(-80, 80) * mm});
            skLineSegment(sketch, "E79.1", {"start": v(-70, 90) * mm, "end": v(70, 90) * mm});
            skArc(sketch, "E79.2", {"start": v(-70, 90) * mm, "mid": v(-77.07, 87.07) * mm, "end": v(-80, 80) * mm});
            skArc(sketch, "E79.3", {"start": v(80, 80) * mm, "mid": v(77.07, 87.07) * mm, "end": v(70, 90) * mm});
            skLineSegment(sketch, "E79.4", {"start": v(80, -80) * mm, "end": v(80, 80) * mm});
            skCircle(sketch, "E79.5", {"center": v(60, 67.5) * mm, "radius": 4 * mm});
            skArc(sketch, "E79.6", {"start": v(70, -90) * mm, "mid": v(77.07, -87.07) * mm, "end": v(80, -80) * mm});
            skCircle(sketch, "E79.7", {"center": v(60, -67.5) * mm, "radius": 4 * mm});
            skLineSegment(sketch, "E79.8", {"start": v(-70, -90) * mm, "end": v(70, -90) * mm});
            skArc(sketch, "E79.10", {"start": v(-80, -80) * mm, "mid": v(-77.07, -87.07) * mm, "end": v(-70, -90) * mm});
            skLineSegment(sketch, "E79.12", {"start": v(-60, 40.3) * mm, "end": v(-60, -40.3) * mm});
            skArc(sketch, "E79.13", {"start": v(-56.15, -48.18) * mm, "mid": v(0, -67.5) * mm, "end": v(56.15, -48.18) * mm});
            skArc(sketch, "E79.14", {"start": v(-60, -40.3) * mm, "mid": v(-58.99, -44.68) * mm, "end": v(-56.15, -48.18) * mm});
            skArc(sketch, "E79.15", {"start": v(56.15, -48.18) * mm, "mid": v(58.99, -44.68) * mm, "end": v(60, -40.3) * mm});
            skLineSegment(sketch, "E79.16", {"start": v(60, 40.3) * mm, "end": v(60, -40.3) * mm});
            skArc(sketch, "E79.17", {"start": v(60, 40.3) * mm, "mid": v(58.99, 44.68) * mm, "end": v(56.15, 48.18) * mm});
            skArc(sketch, "E79.18", {"start": v(56.15, 48.18) * mm, "mid": v(0, 67.5) * mm, "end": v(-56.15, 48.18) * mm});
            skArc(sketch, "E79.19", {"start": v(-56.15, 48.18) * mm, "mid": v(-58.99, 44.68) * mm, "end": v(-60, 40.3) * mm});
            skLineSegment(sketch, "E80", {"start": v(0, 90) * mm, "end": v(0, 120) * mm, "construction": true});
            skCircle(sketch, "E81", {"center": v(0, 120) * mm, "radius": 6 * mm});
            skLineSegment(sketch, "E82", {"start": v(-33, 90) * mm, "end": v(-15, 108) * mm});
            skLineSegment(sketch, "E83", {"start": v(-15, 108) * mm, "end": v(-15, 120) * mm});
            skArc(sketch, "E84", {"start": v(15, 120) * mm, "mid": v(0, 135) * mm, "end": v(-15, 120) * mm});
            skLineSegment(sketch, "E85", {"start": v(15, 120) * mm, "end": v(15, 108) * mm});
            skLineSegment(sketch, "E86", {"start": v(15, 108) * mm, "end": v(33, 90) * mm});
            skLineSegment(sketch, "E87", {"start": v(-80, 0) * mm, "end": v(80, 0) * mm, "construction": true});
            skLineSegment(sketch, "E88.MirrorCS", {"start": v(-33, -90) * mm, "end": v(-15, -108) * mm});
            skLineSegment(sketch, "E89.MirrorCS", {"start": v(-15, -108) * mm, "end": v(-15, -120) * mm});
            skCircle(sketch, "E90.MirrorC", {"center": v(0, -120) * mm, "radius": 6 * mm});
            skLineSegment(sketch, "E91.MirrorCS", {"start": v(15, -120) * mm, "end": v(15, -108) * mm});
            skLineSegment(sketch, "E92.MirrorCS", {"start": v(15, -108) * mm, "end": v(33, -90) * mm});
            skArc(sketch, "E93.MirrorCS", {"start": v(15, -120) * mm, "mid": v(0, -135) * mm, "end": v(-15, -120) * mm});
            skLineSegment(sketch, "E94.MirrorCS", {"start": v(0, -90) * mm, "end": v(0, -120) * mm, "construction": true});
            skSolve(sketch);
        }
        {
            var Q0;
            Q0 = qSketchRegion(id + "F16", true);
            var Q1;
            Q1=makeQuery(id+"F2.opExtrude","CAP_FACE",FACE,{"disambiguationData":[OSD([sQuery(id+"F0.wireOp",EDGE,"E12"),sQuery(id+"F0.wireOp",EDGE,"E13"),sQuery(id+"F0.wireOp",EDGE,"E14"),sQuery(id+"F0.wireOp",EDGE,"E15"),sQuery(id+"F0.wireOp",EDGE,"E17.filletArc"),sQuery(id+"F0.wireOp",EDGE,"E18.filletArc"),sQuery(id+"F0.wireOp",EDGE,"E19.filletArc"),sQuery(id+"F0.wireOp",EDGE,"E20.filletArc"),sQuery(id+"F0.wireOp",EDGE,"E25.0"),sQuery(id+"F0.wireOp",EDGE,"E25.1"),sQuery(id+"F0.wireOp",EDGE,"E25.2"),sQuery(id+"F0.wireOp",EDGE,"E25.3"),sQuery(id+"F0.wireOp",EDGE,"E25.4"),sQuery(id+"F0.wireOp",EDGE,"E25.5"),sQuery(id+"F0.wireOp",EDGE,"E25.6"),sQuery(id+"F0.wireOp",EDGE,"E25.7")])],"isStart":false});
            extrude(context, id + "F17", {"entities" : qUnion([Q0]), "endBound" : BoundingType.UP_TO_SURFACE, "depth" : 25 * mm, "endBoundEntityFace" : qUnion([Q1]), "offsetDistance" : 25 * mm});
        }
    });
